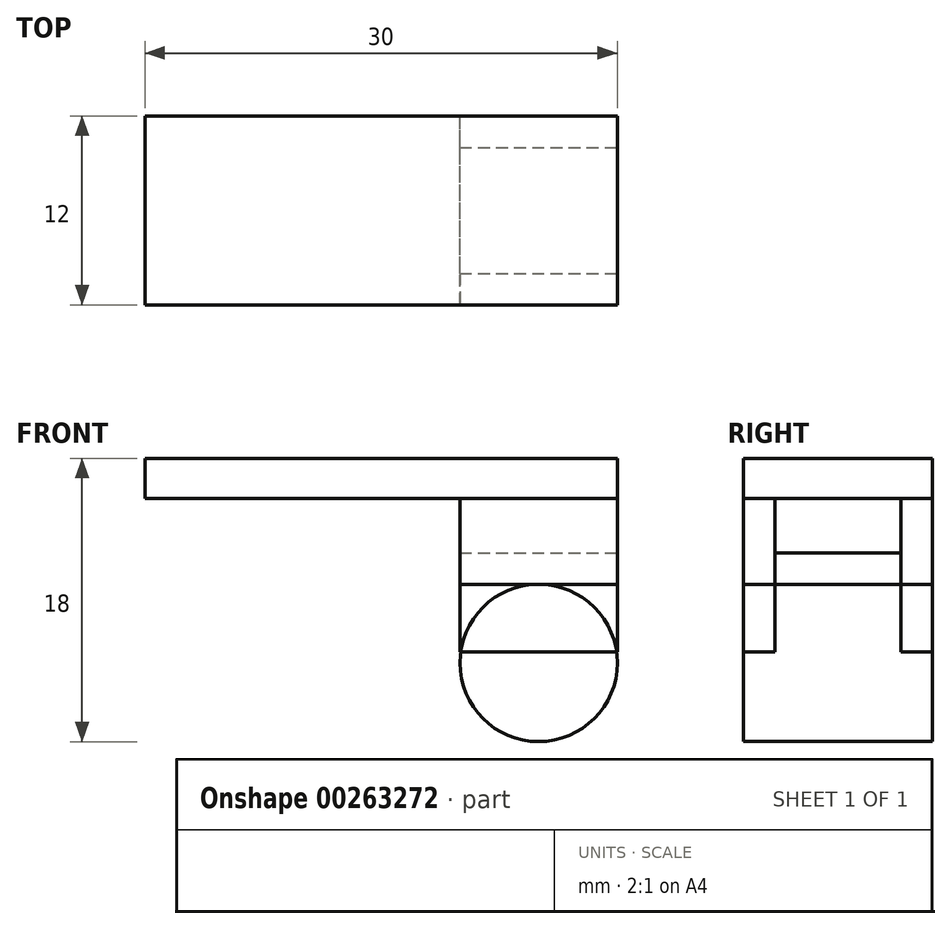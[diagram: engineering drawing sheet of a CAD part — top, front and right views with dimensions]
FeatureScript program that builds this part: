
annotation { "Feature Type Name" : "Feature", "Feature Type Description" : "" }
export const myFeature = defineFeature(function(context is Context, id is Id, definition is map)
    precondition{}
    {
        {
            var Q0;
            Q0=qCreatedBy(makeId("Front.planeOp"),FACE);
            var sketch = newSketch(context, id + "F0", { "sketchPlane" : qUnion([Q0])});
            skLineSegment(sketch, "E0.bottom", {"start": v(-22.8, 12.3) * mm, "end": v(7.2, 12.3) * mm});
            skLineSegment(sketch, "E0.top", {"start": v(-22.8, 9.76) * mm, "end": v(7.2, 9.76) * mm});
            skLineSegment(sketch, "E0.left", {"start": v(-22.8, 12.3) * mm, "end": v(-22.8, 9.76) * mm});
            skLineSegment(sketch, "E0.right", {"start": v(7.2, 12.3) * mm, "end": v(7.2, 9.76) * mm});
            skSolve(sketch);
        }
        {
            var Q0;
            Q0 = qSketchRegion(id + "F0", true);
            extrude(context, id + "F1", {"entities" : qUnion([Q0]), "depth" : 12 * mm});
        }
        {
            var Q0;
            Q0=makeQuery(id+"F1.opExtrude","CAP_FACE",FACE,{"disambiguationData":[OSD([sQuery(id+"F0.wireOp",EDGE,"E0.bottom"),sQuery(id+"F0.wireOp",EDGE,"E0.top"),sQuery(id+"F0.wireOp",EDGE,"E0.left"),sQuery(id+"F0.wireOp",EDGE,"E0.right")])],"isStart":true});
            var sketch = newSketch(context, id + "F2", { "sketchPlane" : qUnion([Q0])});
            skLineSegment(sketch, "E1.bottom", {"start": v(-7.2, 12.3) * mm, "end": v(2.8, 12.3) * mm});
            skLineSegment(sketch, "E1.top", {"start": v(-7.2, 4.3) * mm, "end": v(2.8, 4.3) * mm});
            skLineSegment(sketch, "E1.left", {"start": v(-7.2, 12.3) * mm, "end": v(-7.2, 4.3) * mm});
            skLineSegment(sketch, "E1.right", {"start": v(2.8, 12.3) * mm, "end": v(2.8, 4.3) * mm});
            skSolve(sketch);
        }
        {
            var Q0;
            Q0 = qSketchRegion(id + "F2", true);
            extrude(context, id + "F3", {"entities" : qUnion([Q0]), "operationType" : NewBodyOperationType.ADD, "oppositeDirection" : true, "depth" : 2 * mm});
        }
        {
            var Q0;
            Q0=makeQuery(id+"F3.opExtrude","CAP_FACE",FACE,{"disambiguationData":[OSD([sQuery(id+"F2.wireOp",EDGE,"E1.bottom"),sQuery(id+"F2.wireOp",EDGE,"E1.top"),sQuery(id+"F2.wireOp",EDGE,"E1.left"),sQuery(id+"F2.wireOp",EDGE,"E1.right")])],"isStart":false});
            var sketch = newSketch(context, id + "F4", { "sketchPlane" : qUnion([Q0])});
            skLineSegment(sketch, "E2.bottom", {"start": v(-2.8, 4.3) * mm, "end": v(7.2, 4.3) * mm});
            skLineSegment(sketch, "E2.top", {"start": v(-2.8, 6.3) * mm, "end": v(7.2, 6.3) * mm});
            skLineSegment(sketch, "E2.left", {"start": v(-2.8, 4.3) * mm, "end": v(-2.8, 6.3) * mm});
            skLineSegment(sketch, "E2.right", {"start": v(7.2, 4.3) * mm, "end": v(7.2, 6.3) * mm});
            skSolve(sketch);
        }
        {
            var Q0;
            Q0 = qSketchRegion(id + "F4", true);
            extrude(context, id + "F5", {"entities" : qUnion([Q0]), "operationType" : NewBodyOperationType.ADD, "depth" : 8 * mm});
        }
        {
            var Q0;
            Q0=makeQuery(id+"F1.opExtrude","CAP_FACE",FACE,{"disambiguationData":[OSD([sQuery(id+"F0.wireOp",EDGE,"E0.bottom"),sQuery(id+"F0.wireOp",EDGE,"E0.top"),sQuery(id+"F0.wireOp",EDGE,"E0.left"),sQuery(id+"F0.wireOp",EDGE,"E0.right")])],"isStart":false});
            var sketch = newSketch(context, id + "F6", { "sketchPlane" : qUnion([Q0])});
            skLineSegment(sketch, "E3.bottom", {"start": v(7.2, 12.3) * mm, "end": v(-2.8, 12.3) * mm});
            skLineSegment(sketch, "E3.top", {"start": v(7.2, 4.3) * mm, "end": v(-2.8, 4.3) * mm});
            skLineSegment(sketch, "E3.left", {"start": v(7.2, 12.3) * mm, "end": v(7.2, 4.3) * mm});
            skLineSegment(sketch, "E3.right", {"start": v(-2.8, 12.3) * mm, "end": v(-2.8, 4.3) * mm});
            skSolve(sketch);
        }
        {
            var Q0;
            Q0 = qSketchRegion(id + "F6", true);
            extrude(context, id + "F7", {"entities" : qUnion([Q0]), "operationType" : NewBodyOperationType.ADD, "oppositeDirection" : true, "depth" : 2 * mm});
        }
        {
            var Q0;
            Q0=makeQuery(id+"F3.boolean.opBoolean","MERGE",FACE,{"derivedFrom":[makeQuery(id+"F1.opExtrude","CAP_FACE",FACE,{"disambiguationData":[OSD([sQuery(id+"F0.wireOp",EDGE,"E0.bottom"),sQuery(id+"F0.wireOp",EDGE,"E0.top"),sQuery(id+"F0.wireOp",EDGE,"E0.left"),sQuery(id+"F0.wireOp",EDGE,"E0.right")])],"isStart":true}),makeQuery(id+"F3.opExtrude","CAP_FACE",FACE,{"disambiguationData":[OSD([sQuery(id+"F2.wireOp",EDGE,"E1.bottom"),sQuery(id+"F2.wireOp",EDGE,"E1.top"),sQuery(id+"F2.wireOp",EDGE,"E1.left"),sQuery(id+"F2.wireOp",EDGE,"E1.right")])],"isStart":true})]});
            var sketch = newSketch(context, id + "F8", { "sketchPlane" : qUnion([Q0])});
            skCircle(sketch, "E4", {"center": v(-2.2, -0.7) * mm, "radius": 5 * mm});
            skPoint(sketch, "E4.first.point", {"position": v(-2.2, 4.3) * mm});
            skPoint(sketch, "E4.second.point", {"position": v(-2.2, -5.7) * mm});
            skPoint(sketch, "E4.second.point.positionSnap0", {"position": v(-2.2, 4.3) * mm});
            skPoint(sketch, "E4.third.point", {"position": v(2.8, -0.44) * mm});
            skSolve(sketch);
        }
        {
            var Q0;
            Q0 = qSketchRegion(id + "F8", true);
            extrude(context, id + "F9", {"entities" : qUnion([Q0]), "operationType" : NewBodyOperationType.ADD, "oppositeDirection" : true, "depth" : 12 * mm});
        }
        {
            var Q0;
            Q0=makeQuery(id+"F7.boolean.opBoolean","MERGE",FACE,{"derivedFrom":[makeQuery(id+"F1.opExtrude","CAP_FACE",FACE,{"disambiguationData":[OSD([sQuery(id+"F0.wireOp",EDGE,"E0.bottom"),sQuery(id+"F0.wireOp",EDGE,"E0.top"),sQuery(id+"F0.wireOp",EDGE,"E0.left"),sQuery(id+"F0.wireOp",EDGE,"E0.right")])],"isStart":false}),makeQuery(id+"F7.opExtrude","CAP_FACE",FACE,{"disambiguationData":[OSD([sQuery(id+"F6.wireOp",EDGE,"E3.bottom"),sQuery(id+"F6.wireOp",EDGE,"E3.top"),sQuery(id+"F6.wireOp",EDGE,"E3.left"),sQuery(id+"F6.wireOp",EDGE,"E3.right")])],"isStart":true})]});
            var sketch = newSketch(context, id + "F10", { "sketchPlane" : qUnion([Q0])});
            skLineSegment(sketch, "E5.bottom", {"start": v(-2.8, 9.76) * mm, "end": v(7.2, 9.76) * mm});
            skLineSegment(sketch, "E5.top", {"start": v(-2.8, 0) * mm, "end": v(7.2, 0) * mm});
            skLineSegment(sketch, "E5.left", {"start": v(-2.8, 9.76) * mm, "end": v(-2.8, 0) * mm});
            skLineSegment(sketch, "E5.right", {"start": v(7.2, 9.76) * mm, "end": v(7.2, 0) * mm});
            skSolve(sketch);
        }
        {
            var Q0;
            Q0 = qSketchRegion(id + "F10", true);
            extrude(context, id + "F11", {"entities" : qUnion([Q0]), "oppositeDirection" : true, "depth" : 2 * mm});
        }
        {
            var Q0;
            Q0=makeQuery(id+"F3.boolean.opBoolean","MERGE",FACE,{"derivedFrom":[makeQuery(id+"F1.opExtrude","CAP_FACE",FACE,{"disambiguationData":[OSD([sQuery(id+"F0.wireOp",EDGE,"E0.bottom"),sQuery(id+"F0.wireOp",EDGE,"E0.top"),sQuery(id+"F0.wireOp",EDGE,"E0.left"),sQuery(id+"F0.wireOp",EDGE,"E0.right")])],"isStart":true}),makeQuery(id+"F3.opExtrude","CAP_FACE",FACE,{"disambiguationData":[OSD([sQuery(id+"F2.wireOp",EDGE,"E1.bottom"),sQuery(id+"F2.wireOp",EDGE,"E1.top"),sQuery(id+"F2.wireOp",EDGE,"E1.left"),sQuery(id+"F2.wireOp",EDGE,"E1.right")])],"isStart":true})]});
            var sketch = newSketch(context, id + "F12", { "sketchPlane" : qUnion([Q0])});
            skLineSegment(sketch, "E6.bottom", {"start": v(2.8, 9.76) * mm, "end": v(-7.2, 9.76) * mm});
            skLineSegment(sketch, "E6.top", {"start": v(2.8, 0) * mm, "end": v(-7.2, 0) * mm});
            skLineSegment(sketch, "E6.left", {"start": v(2.8, 9.76) * mm, "end": v(2.8, 0) * mm});
            skLineSegment(sketch, "E6.right", {"start": v(-7.2, 9.76) * mm, "end": v(-7.2, 0) * mm});
            skSolve(sketch);
        }
        {
            var Q0;
            Q0 = qSketchRegion(id + "F12", true);
            extrude(context, id + "F13", {"entities" : qUnion([Q0]), "oppositeDirection" : true, "depth" : 2 * mm});
        }
    });
